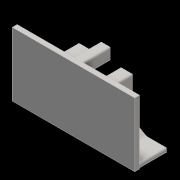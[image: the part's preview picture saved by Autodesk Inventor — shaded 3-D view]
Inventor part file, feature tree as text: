
AUTODESK INVENTOR PART (.ipt)
format: ipt  version: 2016 (Build 200138000, 138)  size: 830,464 bytes
history: native  units: mm
features: sketch x4, extrude x2, chamfer x1, mirror x1
ambient origin geometry x8: Origin, YZ Plane, XZ Plane, XY Plane, X Axis, Y Axis, Z Axis, Center Point
bodies: Solid1 (feature_tree)
feature tree (8):
  sketch  "Sketch1"  dims[d2=13.4mm d3=8.6mm]
  sketch  "Sketch2"  dims[d4=17.4mm]
  extrude  "Extrusion1"  Depth=8.6mm
  chamfer  "Chamfer1"  Distance=1.0mm
  extrude  "Extrusion3"  Depth=5.0mm
  mirror  "Mirror2"
  sketch  "Sketch3"  dims[d5=7.6mm]
  sketch  "Sketch5"  dims[d6=0.5mm d7=1.0mm d10=5.0mm d11=5.0mm d12=0.5mm d15=2.0mm d16=4.0mm d17=4.0mm d18=4.25mm d19=4.25mm d20=13.4mm d23=17.3mm d24=7.5mm d25=4.0mm d28=26.2mm d29=6.1mm d30=2.0mm d31=5.0mm d32=0.5mm d33=5.0mm d34=0.5mm d36=2.0mm d37=0.5mm d40=150.0deg d41=2.0mm d42=11.5mm d43=0.0mm d44=0.5mm d45=2.0mm d46=45.0deg d47=6.1mm d48=7.6mm d51=2.0mm d52=0.0mm]
